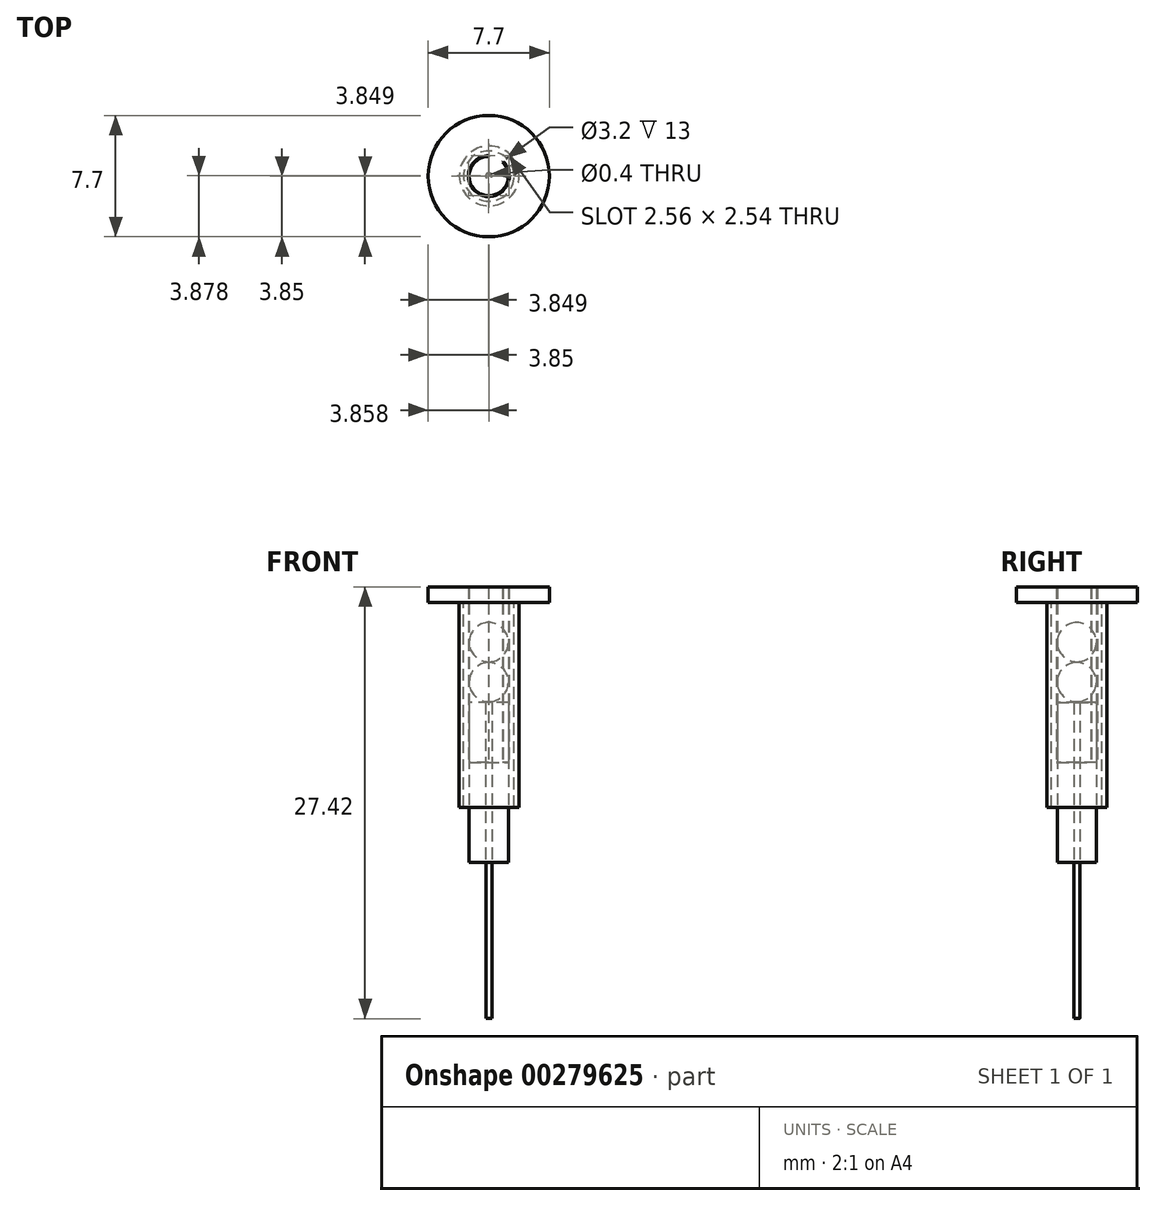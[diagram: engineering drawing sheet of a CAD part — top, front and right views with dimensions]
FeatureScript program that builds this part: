
annotation { "Feature Type Name" : "Feature", "Feature Type Description" : "" }
export const myFeature = defineFeature(function(context is Context, id is Id, definition is map)
    precondition{}
    {
        {
            var Q0;
            Q0=qCreatedBy(makeId("Top.planeOp"),FACE);
            var sketch = newSketch(context, id + "F0", { "sketchPlane" : qUnion([Q0])});
            skCircle(sketch, "E0", {"center": v(0, 0) * mm, "radius": 1.24 * mm});
            skCircle(sketch, "E1", {"center": v(0, 0) * mm, "radius": 0.2 * mm});
            skSolve(sketch);
        }
        {
            var Q0;
            Q0=makeQuery(id+"F0.imprint","IMPRINT",FACE,{"disambiguationData":[TD([[makeQuery(id+"F0.imprint","IMPRINT",EDGE,{"derivedFrom":sQuery(id+"F0.wireOp",EDGE,"E0")}),1.0]])]});
            extrude(context, id + "F1", {"entities" : qUnion([Q0]), "depth" : 10.16 * mm});
        }
        {
            var Q0;
            Q0=qCreatedBy(makeId("Top.planeOp"),FACE);
            var sketch = newSketch(context, id + "F2", { "sketchPlane" : qUnion([Q0])});
            skCircle(sketch, "E2", {"center": v(0, 0) * mm, "radius": 0.2 * mm});
            skSolve(sketch);
        }
        {
            var Q0;
            Q0=makeQuery(id+"F2.imprint","IMPRINT",FACE,{"disambiguationData":[TD([[makeQuery(id+"F2.imprint","IMPRINT",EDGE,{"derivedFrom":sQuery(id+"F2.wireOp",EDGE,"E2")}),1.0]])]});
            extrude(context, id + "F3", {"entities" : qUnion([Q0]), "oppositeDirection" : true, "depth" : 9.9 * mm});
        }
        {
            var Q0;
            Q0=makeQuery(id+"F1.opExtrude","CAP_FACE",FACE,{"disambiguationData":[OSD([sQuery(id+"F0.wireOp",EDGE,"E0"),sQuery(id+"F0.wireOp",EDGE,"E1")])],"isStart":false});
            var sketch = newSketch(context, id + "F4", { "sketchPlane" : qUnion([Q0])});
            skArc(sketch, "E3", {"start": v(0, 1.24) * mm, "mid": v(-0.47, -1.15) * mm, "end": v(0.87, 0.89) * mm});
            skArc(sketch, "E4.0", {"start": v(0, 1.3) * mm, "mid": v(-0.5, -1.2) * mm, "end": v(0.9, 0.93) * mm});
            skLineSegment(sketch, "E5", {"start": v(0, 1.3) * mm, "end": v(0, 1.24) * mm});
            skLineSegment(sketch, "E6", {"start": v(0.9, 0.93) * mm, "end": v(0.87, 0.89) * mm});
            skSolve(sketch);
        }
        {
            var Q0;
            Q0=makeQuery(id+"F4.imprint","IMPRINT",FACE,{"disambiguationData":[TD([[makeQuery(id+"F4.imprint","IMPRINT",EDGE,{"derivedFrom":sQuery(id+"F4.wireOp",EDGE,"E3")}),-1.0]])]});
            extrude(context, id + "F5", {"entities" : qUnion([Q0]), "depth" : 6.35 * mm, "hasSecondDirection" : true, "secondDirectionOppositeDirection" : true, "secondDirectionDepth" : 3.8 * mm});
        }
        {
            var Q0;
            Q0=qCreatedBy(makeId("Front.planeOp"),FACE);
            var sketch = newSketch(context, id + "F6", { "sketchPlane" : qUnion([Q0])});
            skLineSegment(sketch, "E7", {"start": v(0, 10.22) * mm, "end": v(0, 12.7) * mm});
            skArc(sketch, "E8", {"start": v(0, 12.7) * mm, "mid": v(-1.24, 11.47) * mm, "end": v(0, 10.22) * mm});
            skSolve(sketch);
        }
        {
            var Q0;
            Q0=makeQuery(id+"F6.imprint","IMPRINT",FACE,{"disambiguationData":[TD([[makeQuery(id+"F6.imprint","IMPRINT",EDGE,{"derivedFrom":sQuery(id+"F6.wireOp",EDGE,"E7")}),1.0]])]});
            var Q1;
            Q1=sQuery(id+"F6.wireOp",EDGE,"E7");
            revolve(context, id + "F7", {"entities" : qUnion([Q0]), "axis" : qUnion([Q1]), "revolveType" : RevolveType.FULL});
        }
        {
            var Q0;
            Q0=qCreatedBy(makeId("Front.planeOp"),FACE);
            var sketch = newSketch(context, id + "F8", { "sketchPlane" : qUnion([Q0])});
            skLineSegment(sketch, "E9", {"start": v(0, 12.76) * mm, "end": v(0, 15.25) * mm});
            skArc(sketch, "E10", {"start": v(0, 15.25) * mm, "mid": v(1.24, 14) * mm, "end": v(0, 12.76) * mm});
            skSolve(sketch);
        }
        {
            var Q0;
            Q0=makeQuery(id+"F8.imprint","IMPRINT",FACE,{"disambiguationData":[TD([[makeQuery(id+"F8.imprint","IMPRINT",EDGE,{"derivedFrom":sQuery(id+"F8.wireOp",EDGE,"E9")}),-1.0]])]});
            var Q1;
            Q1=sQuery(id+"F8.wireOp",EDGE,"E9");
            revolve(context, id + "F9", {"entities" : qUnion([Q0]), "axis" : qUnion([Q1]), "revolveType" : RevolveType.FULL});
        }
        {
            var Q0;
            Q0=makeQuery(id+"F5.opExtrude","CAP_FACE",FACE,{"disambiguationData":[OSD([sQuery(id+"F4.wireOp",EDGE,"E3"),sQuery(id+"F4.wireOp",EDGE,"E4.0"),sQuery(id+"F4.wireOp",EDGE,"E5"),sQuery(id+"F4.wireOp",EDGE,"E6")])],"isStart":false});
            var sketch = newSketch(context, id + "F10", { "sketchPlane" : qUnion([Q0])});
            skCircle(sketch, "E11", {"center": v(0, 0) * mm, "radius": 3.85 * mm});
            skSolve(sketch);
        }
        {
            var Q0;
            Q0=makeQuery(id+"F10.imprint","IMPRINT",FACE,{"disambiguationData":[TD([[makeQuery(id+"F10.imprint","IMPRINT",EDGE,{"derivedFrom":sQuery(id+"F10.wireOp",EDGE,"E11")}),1.0]])]});
            extrude(context, id + "F11", {"entities" : qUnion([Q0]), "depth" : 1 * mm, "offsetDistance" : 25.4 * mm});
        }
        {
            var Q0;
            Q0=makeQuery(id+"F11.opExtrude","CAP_FACE",FACE,{"disambiguationData":[OSD([sQuery(id+"F4.wireOp",EDGE,"E3"),sQuery(id+"F4.wireOp",EDGE,"E4.0"),sQuery(id+"F4.wireOp",EDGE,"E5"),sQuery(id+"F4.wireOp",EDGE,"E6"),sQuery(id+"F10.wireOp",EDGE,"E11")])],"isStart":true});
            var sketch = newSketch(context, id + "F12", { "sketchPlane" : qUnion([Q0])});
            skCircle(sketch, "E12", {"center": v(0, 0) * mm, "radius": 1.6 * mm});
            skSolve(sketch);
        }
        {
            var Q0;
            Q0=makeQuery(id+"F12.imprint","IMPRINT",FACE,{"disambiguationData":[TD([[makeQuery(id+"F12.imprint","IMPRINT",EDGE,{"derivedFrom":sQuery(id+"F12.wireOp",EDGE,"E12")}),-1.0]])]});
            var sketch = newSketch(context, id + "F13", { "sketchPlane" : qUnion([Q0])});
            skCircle(sketch, "E13", {"center": v(0.02, 0) * mm, "radius": 1.9 * mm});
            skSolve(sketch);
        }
        {
            var Q0;
            Q0=makeQuery(id+"F13.imprint","IMPRINT",FACE,{"disambiguationData":[TD([[makeQuery(id+"F13.imprint","IMPRINT",EDGE,{"derivedFrom":sQuery(id+"F13.wireOp",EDGE,"E13")}),1.0]])]});
            extrude(context, id + "F14", {"entities" : qUnion([Q0]), "operationType" : NewBodyOperationType.ADD, "depth" : 13 * mm, "offsetDistance" : 25.4 * mm});
        }
    });
